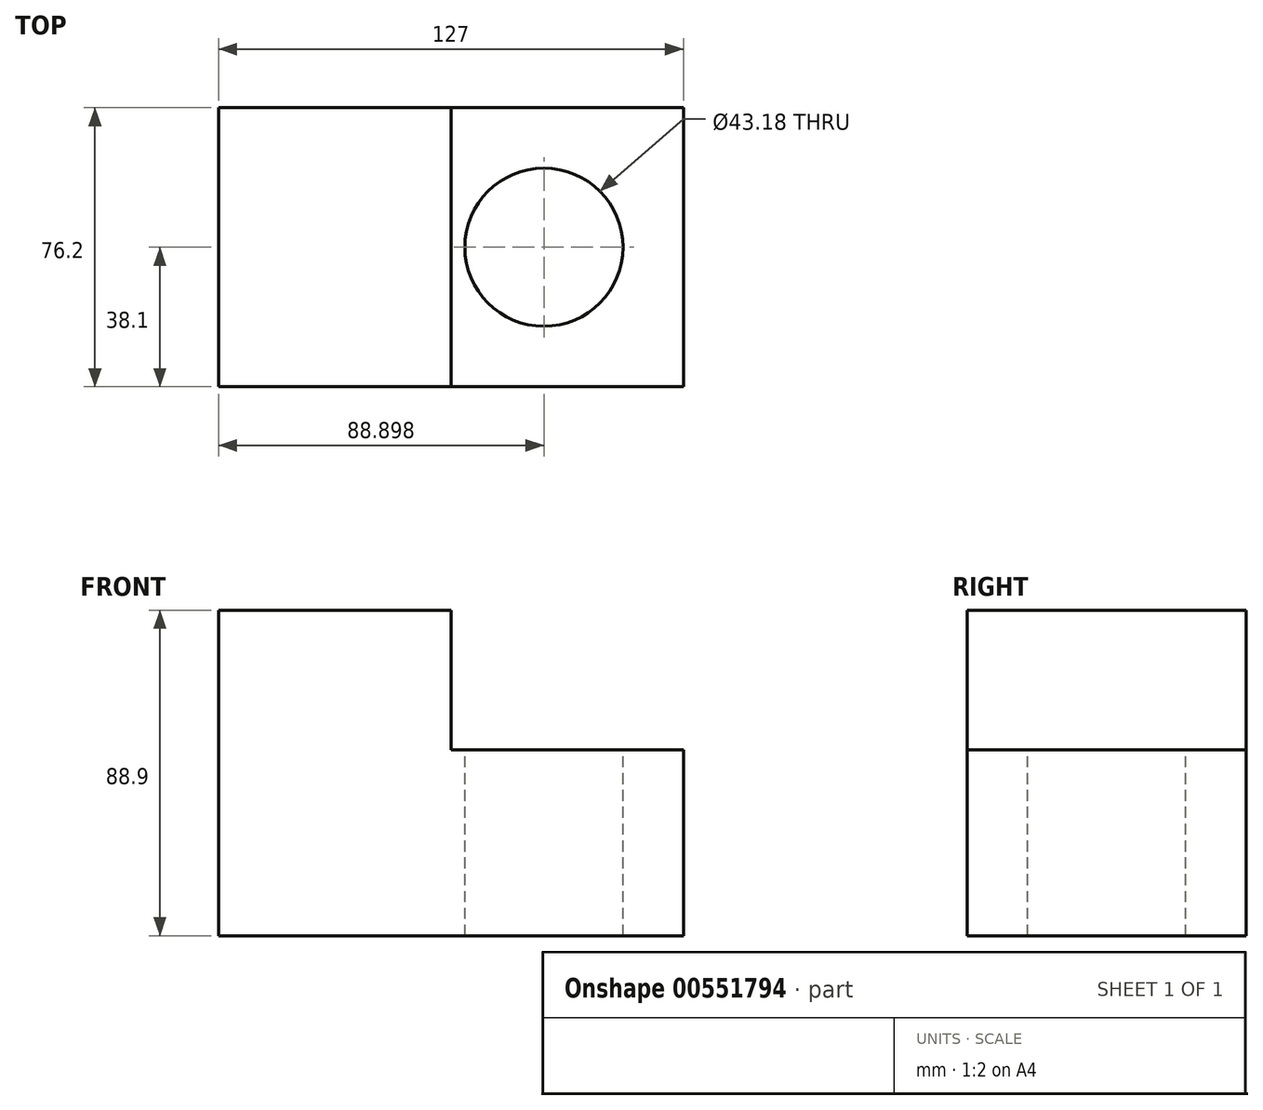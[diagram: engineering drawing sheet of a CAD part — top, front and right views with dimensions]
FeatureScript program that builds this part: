
annotation { "Feature Type Name" : "Feature", "Feature Type Description" : "" }
export const myFeature = defineFeature(function(context is Context, id is Id, definition is map)
    precondition{}
    {
        {
            var Q0;
            Q0=qCreatedBy(makeId("Front.planeOp"),FACE);
            var sketch = newSketch(context, id + "F0", { "sketchPlane" : qUnion([Q0])});
            skLineSegment(sketch, "E0.bottom", {"start": v(-40.32, 63.77) * mm, "end": v(23.18, 63.77) * mm});
            skLineSegment(sketch, "E0.top", {"start": v(-40.32, -25.13) * mm, "end": v(23.18, -25.13) * mm});
            skLineSegment(sketch, "E0.left", {"start": v(-40.32, 63.77) * mm, "end": v(-40.32, -25.13) * mm});
            skLineSegment(sketch, "E0.right", {"start": v(23.18, 63.77) * mm, "end": v(23.18, 25.67) * mm});
            skLineSegment(sketch, "E1", {"start": v(23.18, 25.67) * mm, "end": v(86.68, 25.67) * mm});
            skLineSegment(sketch, "E2", {"start": v(86.68, 25.67) * mm, "end": v(86.68, -25.13) * mm});
            skLineSegment(sketch, "E3", {"start": v(86.68, -25.13) * mm, "end": v(23.18, -25.13) * mm});
            skSolve(sketch);
        }
        {
            var Q0;
            Q0=makeQuery(id+"F0.imprint","IMPRINT",FACE,{"disambiguationData":[TD([[makeQuery(id+"F0.imprint","IMPRINT",EDGE,{"derivedFrom":sQuery(id+"F0.wireOp",EDGE,"E0.bottom")}),-1.0]])]});
            var Q1;
            Q1=sQuery(id+"F0.wireOp",EDGE,"E0.bottom");
            var Q2;
            Q2=sQuery(id+"F0.wireOp",EDGE,"E0.top");
            var Q3;
            Q3=sQuery(id+"F0.wireOp",EDGE,"E0.right");
            extrude(context, id + "F1", {"entities" : qUnion([Q0]), "surfaceEntities" : qUnion([Q1, Q2, Q3]), "depth" : 38.1 * mm, "offsetDistance" : 25.4 * mm, "hasSecondDirection" : true, "secondDirectionOppositeDirection" : true, "secondDirectionDepth" : 38.1 * mm});
        }
        {
            var Q0;
            Q0=makeQuery(id+"F1.opExtrude","SWEPT_FACE",FACE,{"disambiguationData":[OSD([sQuery(id+"F0.wireOp",EDGE,"E1")])]});
            var sketch = newSketch(context, id + "F2", { "sketchPlane" : qUnion([Q0])});
            skCircle(sketch, "E4", {"center": v(48.58, 0) * mm, "radius": 21.59 * mm});
            skSolve(sketch);
        }
        {
            var Q0;
            Q0=qSketchRegion(id+"F2",true);
            extrude(context, id + "F3", {"entities" : qUnion([Q0]), "operationType" : NewBodyOperationType.REMOVE, "endBound" : BoundingType.UP_TO_NEXT, "oppositeDirection" : true, "depth" : 25.4 * mm, "offsetDistance" : 25.4 * mm});
        }
    });
